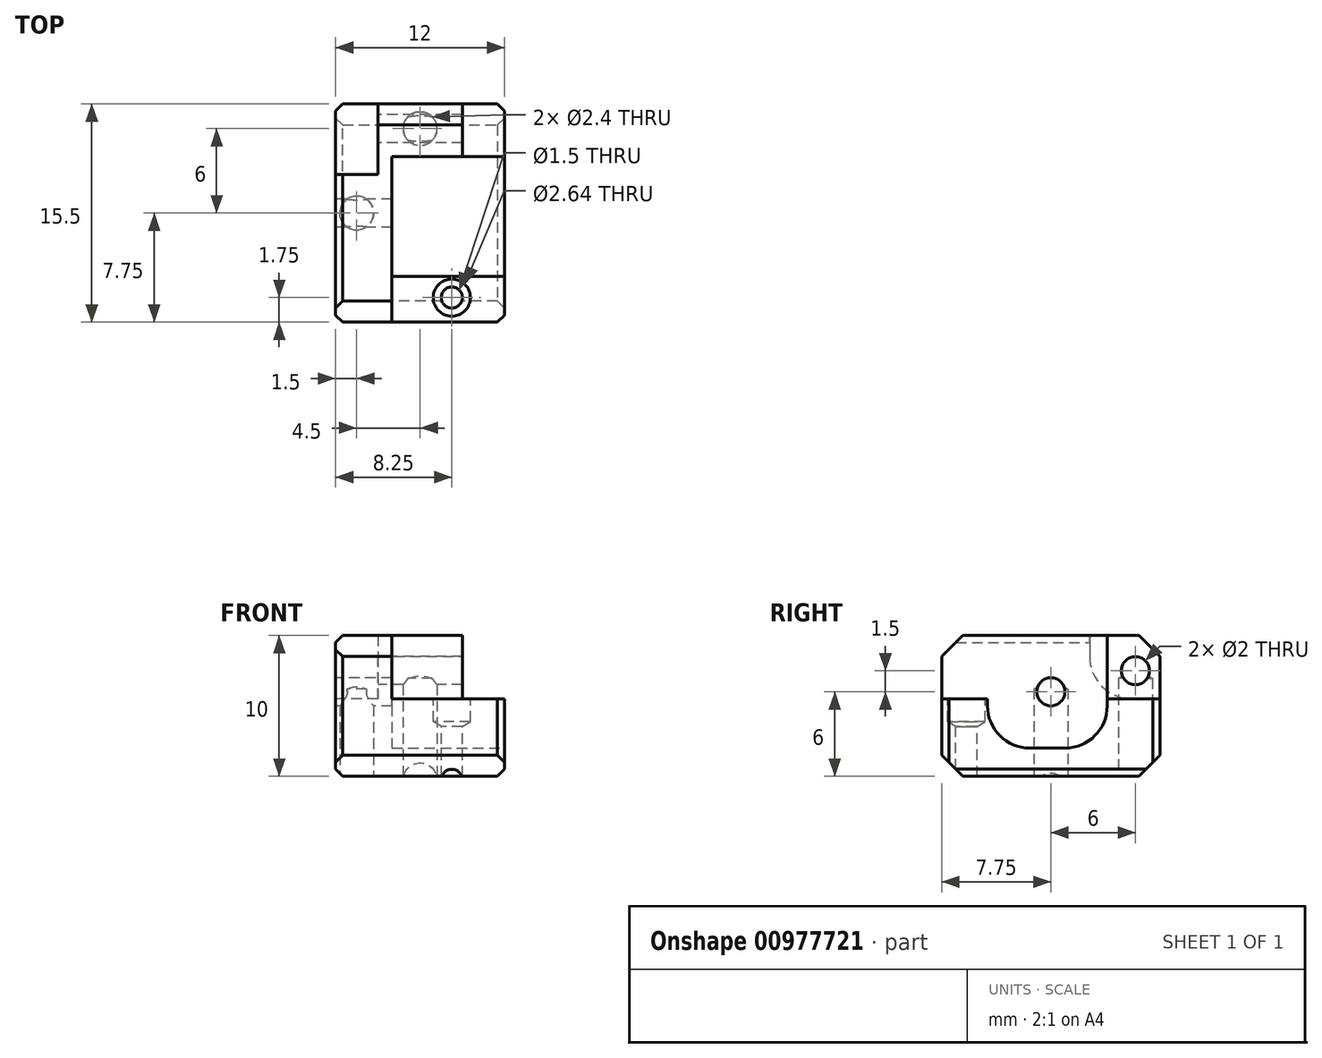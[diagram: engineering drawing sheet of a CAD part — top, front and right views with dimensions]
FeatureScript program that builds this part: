
annotation { "Feature Type Name" : "Feature", "Feature Type Description" : "" }
export const myFeature = defineFeature(function(context is Context, id is Id, definition is map)
    precondition{}
    {
        {
            var Q0;
            Q0=qCreatedBy(makeId("Top.planeOp"),FACE);
            var sketch = newSketch(context, id + "F0", { "sketchPlane" : qUnion([Q0])});
            skLineSegment(sketch, "E0.bottom", {"start": v(-6, 7.75) * mm, "end": v(6, 7.75) * mm});
            skLineSegment(sketch, "E0.top", {"start": v(-6, -7.75) * mm, "end": v(6, -7.75) * mm});
            skLineSegment(sketch, "E0.left", {"start": v(-6, 7.75) * mm, "end": v(-6, -7.75) * mm});
            skLineSegment(sketch, "E0.right", {"start": v(6, 7.75) * mm, "end": v(6, -7.75) * mm});
            skLineSegment(sketch, "E1", {"start": v(-5.73, 0) * mm, "end": v(20.72, 0) * mm, "construction": true});
            skLineSegment(sketch, "E2", {"start": v(0, -9.66) * mm, "end": v(0, 15.88) * mm, "construction": true});
            skSolve(sketch);
        }
        {
            var Q0;
            Q0 = qSketchRegion(id + "F0", true);
            extrude(context, id + "F1", {"entities" : qUnion([Q0]), "depth" : 10 * mm, "offsetDistance" : 25 * mm});
        }
        {
            var Q0;
            Q0=makeQuery(id+"F1.opExtrude","CAP_FACE",FACE,{"disambiguationData":[OSD([sQuery(id+"F0.wireOp",EDGE,"E0.bottom"),sQuery(id+"F0.wireOp",EDGE,"E0.top"),sQuery(id+"F0.wireOp",EDGE,"E0.left"),sQuery(id+"F0.wireOp",EDGE,"E0.right")])],"isStart":false});
            var sketch = newSketch(context, id + "F2", { "sketchPlane" : qUnion([Q0])});
            skLineSegment(sketch, "E3.bottom", {"start": v(6, -7.75) * mm, "end": v(-2, -7.75) * mm});
            skLineSegment(sketch, "E3.left", {"start": v(6, -7.75) * mm, "end": v(6, 7.75) * mm});
            skLineSegment(sketch, "E3.right", {"start": v(-2, -7.75) * mm, "end": v(-2, 4) * mm});
            skLineSegment(sketch, "E4", {"start": v(6, 7.75) * mm, "end": v(3, 7.75) * mm});
            skLineSegment(sketch, "E5", {"start": v(3, 7.75) * mm, "end": v(3, 4) * mm});
            skLineSegment(sketch, "E6", {"start": v(3, 4) * mm, "end": v(-2, 4) * mm});
            skSolve(sketch);
        }
        {
            var Q0;
            Q0 = qSketchRegion(id + "F2", true);
            extrude(context, id + "F3", {"entities" : qUnion([Q0]), "operationType" : NewBodyOperationType.REMOVE, "oppositeDirection" : true, "depth" : (10 - 5.5) * mm, "offsetDistance" : 25 * mm});
        }
        {
            var Q0;
            Q0=makeQuery(id+"F1.opExtrude","SWEPT_FACE",FACE,{"disambiguationData":[OSD([sQuery(id+"F0.wireOp",EDGE,"E0.right")])]});
            var sketch = newSketch(context, id + "F4", { "sketchPlane" : qUnion([Q0])});
            skLineSegment(sketch, "E7.bottom", {"start": v(-4.5, 5.5) * mm, "end": v(4, 5.5) * mm});
            skLineSegment(sketch, "E7.top", {"start": v(-4.5, 2) * mm, "end": v(4, 2) * mm});
            skLineSegment(sketch, "E7.left", {"start": v(-4.5, 5.5) * mm, "end": v(-4.5, 2) * mm});
            skLineSegment(sketch, "E7.right", {"start": v(4, 5.5) * mm, "end": v(4, 2) * mm});
            skSolve(sketch);
        }
        {
            var Q0;
            Q0 = qSketchRegion(id + "F4", true);
            extrude(context, id + "F5", {"entities" : qUnion([Q0]), "operationType" : NewBodyOperationType.REMOVE, "oppositeDirection" : true, "depth" : 8 * mm, "offsetDistance" : 25 * mm});
        }
        {
            var Q0;
            Q0=makeQuery(id+"F5.boolean.opBoolean","COPY",EDGE,{"derivedFrom":makeQuery(id+"F5.opExtrude","SWEPT_EDGE",EDGE,{"disambiguationData":[OSD([sQuery(id+"F4.wireOp",EDGE,"E7.top"),sQuery(id+"F4.wireOp",EDGE,"E7.right")])]})});
            var Q1;
            Q1=makeQuery(id+"F5.boolean.opBoolean","COPY",EDGE,{"derivedFrom":makeQuery(id+"F5.opExtrude","SWEPT_EDGE",EDGE,{"disambiguationData":[OSD([sQuery(id+"F4.wireOp",EDGE,"E7.top"),sQuery(id+"F4.wireOp",EDGE,"E7.left")])]})});
            fillet(context, id + "F6", {"entities" : qUnion([Q0, Q1]), "radius" : 3 * mm, "tangentPropagation" : true, "allowEdgeOverflow" : false});
        }
        {
            var Q0;
            Q0=makeQuery(id+"F1.opExtrude","CAP_EDGE",EDGE,{"disambiguationData":[OSD([sQuery(id+"F0.wireOp",EDGE,"E0.bottom")])],"isStart":false});
            var Q1;
            Q1=makeQuery(id+"F1.opExtrude","CAP_EDGE",EDGE,{"disambiguationData":[OSD([sQuery(id+"F0.wireOp",EDGE,"E0.top")])],"isStart":true});
            var Q2;
            Q2=makeQuery(id+"F1.opExtrude","CAP_EDGE",EDGE,{"disambiguationData":[OSD([sQuery(id+"F0.wireOp",EDGE,"E0.top")])],"isStart":false});
            var Q3;
            Q3=makeQuery(id+"F1.opExtrude","CAP_EDGE",EDGE,{"disambiguationData":[OSD([sQuery(id+"F0.wireOp",EDGE,"E0.bottom")])],"isStart":true});
            chamfer(context, id + "F7", {"entities" : qUnion([Q0, Q1, Q2, Q3]), "width" : 1.5 * mm, "tangentPropagation" : true});
        }
        {
            var Q0;
            Q0=makeQuery(id+"F1.opExtrude","SWEPT_FACE",FACE,{"disambiguationData":[OSD([sQuery(id+"F0.wireOp",EDGE,"E0.left")])]});
            var sketch = newSketch(context, id + "F8", { "sketchPlane" : qUnion([Q0])});
            skPoint(sketch, "E8", {"position": v(0, 6) * mm});
            skSolve(sketch);
        }
        {
            var Q0;
            Q0=sQuery(id+"F8.wireOp",VERTEX,"E8");
            var Q1;
            Q1=makeQuery(id+"F1.opExtrude","SWEPT_BODY",BODY,{"disambiguationData":[OSD([sQuery(id+"F0.wireOp",EDGE,"E0.bottom"),sQuery(id+"F0.wireOp",EDGE,"E0.top"),sQuery(id+"F0.wireOp",EDGE,"E0.left"),sQuery(id+"F0.wireOp",EDGE,"E0.right")])]});
            hole(context, id + "F9", {"style" : HoleStyle.SIMPLE, "endStyle" : HoleEndStyle.BLIND, "holeDiameter" : 2 * mm, "majorDiameter" : 5 * mm, "holeDepth" : 3 * mm, "isTappedThrough" : true, "tappedDepth" : 12 * mm, "tapClearance" : 3, "locations" : qUnion([Q0]), "scope" : qUnion([Q1])});
        }
        {
            var Q0;
            Q0=makeQuery(id+"F1.opExtrude","SWEPT_FACE",FACE,{"disambiguationData":[OSD([sQuery(id+"F0.wireOp",EDGE,"E0.left")])]});
            var sketch = newSketch(context, id + "F10", { "sketchPlane" : qUnion([Q0])});
            skPoint(sketch, "E9", {"position": v(0, 6) * mm});
            skSolve(sketch);
        }
        {
            var Q0;
            Q0=sQuery(id+"F10.wireOp",VERTEX,"E9");
            var Q1;
            Q1=makeQuery(id+"F1.opExtrude","SWEPT_BODY",BODY,{"disambiguationData":[OSD([sQuery(id+"F0.wireOp",EDGE,"E0.bottom"),sQuery(id+"F0.wireOp",EDGE,"E0.top"),sQuery(id+"F0.wireOp",EDGE,"E0.left"),sQuery(id+"F0.wireOp",EDGE,"E0.right")])]});
            hole(context, id + "F11", {"style" : HoleStyle.SIMPLE, "endStyle" : HoleEndStyle.THROUGH, "holeDiameter" : 2 * mm, "majorDiameter" : 5 * mm, "isTappedThrough" : true, "tappedDepth" : 12 * mm, "tapClearance" : 3, "locations" : qUnion([Q0]), "scope" : qUnion([Q1])});
        }
        {
            var Q0;
            Q0=makeQuery(id+"F1.opExtrude","SWEPT_FACE",FACE,{"disambiguationData":[OSD([sQuery(id+"F0.wireOp",EDGE,"E0.left")])]});
            var sketch = newSketch(context, id + "F12", { "sketchPlane" : qUnion([Q0])});
            skLineSegment(sketch, "E10.bottom", {"start": v(-2.75, 10) * mm, "end": v(-7.75, 10) * mm});
            skLineSegment(sketch, "E10.top", {"start": v(-2.75, 5.5) * mm, "end": v(-7.75, 5.5) * mm});
            skLineSegment(sketch, "E10.left", {"start": v(-2.75, 10) * mm, "end": v(-2.75, 5.5) * mm});
            skLineSegment(sketch, "E10.right", {"start": v(-7.75, 10) * mm, "end": v(-7.75, 5.5) * mm});
            skSolve(sketch);
        }
        {
            var Q0;
            Q0 = qSketchRegion(id + "F12", true);
            extrude(context, id + "F13", {"entities" : qUnion([Q0]), "operationType" : NewBodyOperationType.REMOVE, "oppositeDirection" : true, "depth" : (12 - 3 - 6) * mm, "offsetDistance" : 25 * mm});
        }
        {
            var Q0;
            Q0=makeQuery(id+"F13.boolean.opBoolean","COPY",EDGE,{"derivedFrom":makeQuery(id+"F13.opExtrude","SWEPT_EDGE",EDGE,{"disambiguationData":[OSD([sQuery(id+"F12.wireOp",EDGE,"E10.top"),sQuery(id+"F12.wireOp",EDGE,"E10.left")])]})});
            fillet(context, id + "F14", {"entities" : qUnion([Q0]), "radius" : 3 * mm, "tangentPropagation" : true, "allowEdgeOverflow" : false});
        }
        {
            var Q0;
            Q0=makeQuery(id+"F13.boolean.opBoolean","COPY",FACE,{"derivedFrom":makeQuery(id+"F13.opExtrude","CAP_FACE",FACE,{"disambiguationData":[OSD([sQuery(id+"F12.wireOp",EDGE,"E10.bottom"),sQuery(id+"F12.wireOp",EDGE,"E10.top"),sQuery(id+"F12.wireOp",EDGE,"E10.left"),sQuery(id+"F12.wireOp",EDGE,"E10.right")])],"isStart":false})});
            var sketch = newSketch(context, id + "F15", { "sketchPlane" : qUnion([Q0])});
            skPoint(sketch, "E11", {"position": v(-6, 7.5) * mm});
            skSolve(sketch);
        }
        {
            var Q0;
            Q0=sQuery(id+"F15.wireOp",VERTEX,"E11");
            var Q1;
            Q1=makeQuery(id+"F1.opExtrude","SWEPT_BODY",BODY,{"disambiguationData":[OSD([sQuery(id+"F0.wireOp",EDGE,"E0.bottom"),sQuery(id+"F0.wireOp",EDGE,"E0.top"),sQuery(id+"F0.wireOp",EDGE,"E0.left"),sQuery(id+"F0.wireOp",EDGE,"E0.right")])]});
            hole(context, id + "F16", {"style" : HoleStyle.SIMPLE, "endStyle" : HoleEndStyle.THROUGH, "holeDiameter" : 2 * mm, "majorDiameter" : 5 * mm, "isTappedThrough" : true, "tappedDepth" : 12 * mm, "tapClearance" : 3, "locations" : qUnion([Q0]), "scope" : qUnion([Q1])});
        }
        {
            var Q0;
            {var subQ1=sQuery(id+"F2.wireOp",EDGE,"E3.right");Q0=makeQuery(id+"F5.boolean.opBoolean","SPLIT",FACE,{"disambiguationData":[TD([makeQuery(id+"F1.opExtrude","SWEPT_FACE",FACE,{"disambiguationData":[OSD([sQuery(id+"F0.wireOp",EDGE,"E0.top")])]})])],"derivedFrom":makeQuery(id+"F3.boolean.opBoolean","COPY",FACE,{"derivedFrom":makeQuery(id+"F3.opExtrude","CAP_FACE",FACE,{"disambiguationData":[OSD([sQuery(id+"F2.wireOp",EDGE,"E3.bottom"),sQuery(id+"F2.wireOp",EDGE,"E3.left"),subQ1,sQuery(id+"F2.wireOp",EDGE,"E4"),sQuery(id+"F2.wireOp",EDGE,"E5"),sQuery(id+"F2.wireOp",EDGE,"E6")])],"isStart":false})})});}
            var sketch = newSketch(context, id + "F17", { "sketchPlane" : qUnion([Q0])});
            skPoint(sketch, "E12", {"position": v(2.25, -6) * mm});
            skSolve(sketch);
        }
        {
            var Q0;
            Q0=sQuery(id+"F17.wireOp",VERTEX,"E12");
            var Q1;
            Q1=makeQuery(id+"F1.opExtrude","SWEPT_BODY",BODY,{"disambiguationData":[OSD([sQuery(id+"F0.wireOp",EDGE,"E0.bottom"),sQuery(id+"F0.wireOp",EDGE,"E0.top"),sQuery(id+"F0.wireOp",EDGE,"E0.left"),sQuery(id+"F0.wireOp",EDGE,"E0.right")])]});
            hole(context, id + "F18", {"style" : HoleStyle.SIMPLE, "endStyle" : HoleEndStyle.THROUGH, "holeDiameter" : 1.5 * mm, "majorDiameter" : 5 * mm, "isTappedThrough" : true, "tappedDepth" : 12 * mm, "tapClearance" : 3, "locations" : qUnion([Q0]), "scope" : qUnion([Q1])});
        }
        {
            var Q0;
            {var subQ1=sQuery(id+"F2.wireOp",EDGE,"E3.right");Q0=makeQuery(id+"F5.boolean.opBoolean","SPLIT",FACE,{"disambiguationData":[TD([makeQuery(id+"F1.opExtrude","SWEPT_FACE",FACE,{"disambiguationData":[OSD([sQuery(id+"F0.wireOp",EDGE,"E0.top")])]})])],"derivedFrom":makeQuery(id+"F3.boolean.opBoolean","COPY",FACE,{"derivedFrom":makeQuery(id+"F3.opExtrude","CAP_FACE",FACE,{"disambiguationData":[OSD([sQuery(id+"F2.wireOp",EDGE,"E3.bottom"),sQuery(id+"F2.wireOp",EDGE,"E3.left"),subQ1,sQuery(id+"F2.wireOp",EDGE,"E4"),sQuery(id+"F2.wireOp",EDGE,"E5"),sQuery(id+"F2.wireOp",EDGE,"E6")])],"isStart":false})})});}
            var sketch = newSketch(context, id + "F19", { "sketchPlane" : qUnion([Q0])});
            skPoint(sketch, "E13", {"position": v(2.25, -6) * mm});
            skSolve(sketch);
        }
        {
            var Q0;
            Q0=sQuery(id+"F19.wireOp",VERTEX,"E13");
            var Q1;
            Q1=makeQuery(id+"F1.opExtrude","SWEPT_BODY",BODY,{"disambiguationData":[OSD([sQuery(id+"F0.wireOp",EDGE,"E0.bottom"),sQuery(id+"F0.wireOp",EDGE,"E0.top"),sQuery(id+"F0.wireOp",EDGE,"E0.left"),sQuery(id+"F0.wireOp",EDGE,"E0.right")])]});
            hole(context, id + "F20", {"style" : HoleStyle.SIMPLE, "endStyle" : HoleEndStyle.BLIND, "holeDiameter" : 2.64 * mm, "majorDiameter" : 5 * mm, "holeDepth" : 1.62 * mm, "isTappedThrough" : true, "tappedDepth" : 12 * mm, "tapClearance" : 3, "locations" : qUnion([Q0]), "scope" : qUnion([Q1])});
        }
        {
            var Q0;
            Q0=makeQuery(id+"F1.opExtrude","CAP_EDGE",EDGE,{"disambiguationData":[OSD([sQuery(id+"F0.wireOp",EDGE,"E0.left")])],"isStart":false});
            var Q1;
            {var subQ0=sQuery(id+"F2.wireOp",EDGE,"E3.left");Q1=makeQuery(id+"F5.boolean.opBoolean","SPLIT",EDGE,{"disambiguationData":[TD([makeQuery(id+"F1.opExtrude","SWEPT_FACE",FACE,{"disambiguationData":[OSD([sQuery(id+"F0.wireOp",EDGE,"E0.top")])]})])],"derivedFrom":makeQuery(id+"F3.boolean.opBoolean","COPY",EDGE,{"derivedFrom":makeQuery(id+"F3.opExtrude","CAP_EDGE",EDGE,{"disambiguationData":[OSD([subQ0])],"isStart":false})})});}
            var Q2;
            {var subQ1=sQuery(id+"F2.wireOp",EDGE,"E3.left");Q2=makeQuery(id+"F5.boolean.opBoolean","SPLIT",EDGE,{"disambiguationData":[TD([makeQuery(id+"F1.opExtrude","SWEPT_FACE",FACE,{"disambiguationData":[OSD([sQuery(id+"F0.wireOp",EDGE,"E0.bottom")])]})])],"derivedFrom":makeQuery(id+"F3.boolean.opBoolean","COPY",EDGE,{"derivedFrom":makeQuery(id+"F3.opExtrude","CAP_EDGE",EDGE,{"disambiguationData":[OSD([subQ1])],"isStart":false})})});}
            var Q3;
            Q3=makeQuery(id+"F1.opExtrude","SWEPT_EDGE",EDGE,{"disambiguationData":[OSD([sQuery(id+"F0.wireOp",EDGE,"E0.bottom"),sQuery(id+"F0.wireOp",EDGE,"E0.right")])]});
            var Q4;
            Q4=makeQuery(id+"F1.opExtrude","CAP_EDGE",EDGE,{"disambiguationData":[OSD([sQuery(id+"F0.wireOp",EDGE,"E0.right")])],"isStart":true});
            var Q5;
            Q5=makeQuery(id+"F1.opExtrude","CAP_EDGE",EDGE,{"disambiguationData":[OSD([sQuery(id+"F0.wireOp",EDGE,"E0.left")])],"isStart":true});
            var Q6;
            Q6=makeQuery(id+"F1.opExtrude","SWEPT_EDGE",EDGE,{"disambiguationData":[OSD([sQuery(id+"F0.wireOp",EDGE,"E0.top"),sQuery(id+"F0.wireOp",EDGE,"E0.left")])]});
            var Q7;
            Q7=makeQuery(id+"F1.opExtrude","SWEPT_EDGE",EDGE,{"disambiguationData":[OSD([sQuery(id+"F0.wireOp",EDGE,"E0.bottom"),sQuery(id+"F0.wireOp",EDGE,"E0.left")])]});
            var Q8;
            Q8=makeQuery(id+"F1.opExtrude","SWEPT_EDGE",EDGE,{"disambiguationData":[OSD([sQuery(id+"F0.wireOp",EDGE,"E0.top"),sQuery(id+"F0.wireOp",EDGE,"E0.right")])]});
            chamfer(context, id + "F21", {"entities" : qUnion([Q0, Q1, Q2, Q3, Q4, Q5, Q6, Q7, Q8]), "width" : 0.5 * mm, "tangentPropagation" : true});
        }
        {
            var Q0;
            Q0=makeQuery(id+"F1.opExtrude","CAP_FACE",FACE,{"disambiguationData":[OSD([sQuery(id+"F0.wireOp",EDGE,"E0.bottom"),sQuery(id+"F0.wireOp",EDGE,"E0.top"),sQuery(id+"F0.wireOp",EDGE,"E0.left"),sQuery(id+"F0.wireOp",EDGE,"E0.right")])],"isStart":true});
            var sketch = newSketch(context, id + "F22", { "sketchPlane" : qUnion([Q0])});
            skPoint(sketch, "E14", {"position": v(-4.5, 0) * mm});
            skSolve(sketch);
        }
        {
            var Q0;
            Q0=sQuery(id+"F22.wireOp",VERTEX,"E14");
            var Q1;
            Q1=makeQuery(id+"F1.opExtrude","SWEPT_BODY",BODY,{"disambiguationData":[OSD([sQuery(id+"F0.wireOp",EDGE,"E0.bottom"),sQuery(id+"F0.wireOp",EDGE,"E0.top"),sQuery(id+"F0.wireOp",EDGE,"E0.left"),sQuery(id+"F0.wireOp",EDGE,"E0.right")])]});
            hole(context, id + "F23", {"style" : HoleStyle.SIMPLE, "endStyle" : HoleEndStyle.BLIND, "standardTappedOrClearance" : lookupTablePath({ "fit" : "Normal", "standard" : "ISO", "size" : "M2", "type" : "Clearance" }), "standardBlindInLast" : lookupTablePath({ "fit" : "Normal", "standard" : "ISO", "engagement" : "75%", "pitch" : "0.25 mm", "size" : "M2", "type" : "Clearance & tapped" }), "holeDiameter" : 2.4 * mm, "majorDiameter" : 5 * mm, "holeDepth" : 6 * mm, "isTappedThrough" : true, "tappedDepth" : 12 * mm, "tapClearance" : 3, "locations" : qUnion([Q0]), "scope" : qUnion([Q1])});
        }
        {
            var Q0;
            Q0=makeQuery(id+"F1.opExtrude","CAP_FACE",FACE,{"disambiguationData":[OSD([sQuery(id+"F0.wireOp",EDGE,"E0.bottom"),sQuery(id+"F0.wireOp",EDGE,"E0.top"),sQuery(id+"F0.wireOp",EDGE,"E0.left"),sQuery(id+"F0.wireOp",EDGE,"E0.right")])],"isStart":true});
            var sketch = newSketch(context, id + "F24", { "sketchPlane" : qUnion([Q0])});
            skPoint(sketch, "E15", {"position": v(0, -6) * mm});
            skSolve(sketch);
        }
        {
            var Q0;
            Q0=sQuery(id+"F24.wireOp",VERTEX,"E15");
            var Q1;
            Q1=makeQuery(id+"F1.opExtrude","SWEPT_BODY",BODY,{"disambiguationData":[OSD([sQuery(id+"F0.wireOp",EDGE,"E0.bottom"),sQuery(id+"F0.wireOp",EDGE,"E0.top"),sQuery(id+"F0.wireOp",EDGE,"E0.left"),sQuery(id+"F0.wireOp",EDGE,"E0.right")])]});
            hole(context, id + "F25", {"style" : HoleStyle.SIMPLE, "endStyle" : HoleEndStyle.BLIND, "standardTappedOrClearance" : lookupTablePath({ "fit" : "Normal", "standard" : "ISO", "size" : "M2", "type" : "Clearance" }), "standardBlindInLast" : lookupTablePath({ "fit" : "Normal", "standard" : "ISO", "engagement" : "75%", "pitch" : "0.25 mm", "size" : "M2", "type" : "Clearance & tapped" }), "holeDiameter" : 2.4 * mm, "majorDiameter" : 2 * mm, "holeDepth" : 6 * mm, "isTappedThrough" : true, "tappedDepth" : 12 * mm, "tapClearance" : 3, "locations" : qUnion([Q0]), "scope" : qUnion([Q1])});
        }
    });
